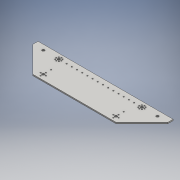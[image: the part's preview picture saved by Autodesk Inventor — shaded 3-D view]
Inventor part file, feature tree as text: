
AUTODESK INVENTOR PART (.ipt)
format: ipt  version: 2016 (Build 200138000, 138)  size: 163,840 bytes
history: native  units: mm
features: reference x46, sketch x2, hole x2, extrude x1
ambient origin geometry x8: Origin, YZ Plane, XZ Plane, XY Plane, X Axis, Y Axis, Z Axis, Center Point
bodies: Body1 (feature_tree)
feature tree (51):
  extrude  "Extrusion2"  Depth=96.0mm
  sketch  "Sketch2"  dims[d0=416.0mm d1=96.0mm]
  sketch  "Sketch3"  dims[d4=4.0mm d5=0.0mm d6=8.0mm d7=6.0mm d8=4.0mm d9=2.0mm d10=90.0deg d11=8.0mm d12=20.594885mm d13=3.7mm d14=6.0mm d15=4.0mm d16=2.0mm d17=90.0deg d18=8.0mm d19=20.594885mm d22=16.0mm d23=80.0mm d24=16.0mm]
  hole  "Hole1"  [1 undecoded]
  hole  "Hole2"  [1 undecoded]
  reference  "Reference1"
  reference  "Reference2"
  reference  "Reference3"
  reference  "Reference4"
  reference  "Reference5"
  reference  "Reference6"
  reference  "Reference7"
  reference  "Reference8"
  reference  "Reference9"
  reference  "Reference10"
  reference  "Reference11"
  reference  "Reference12"
  reference  "Reference13"
  reference  "Reference14"
  reference  "Reference15"
  reference  "Reference16"
  reference  "Reference17"
  reference  "Reference18"
  reference  "Reference19"
  reference  "Reference20"
  reference  "Reference21"
  reference  "Reference22"
  reference  "Reference23"
  reference  "Reference24"
  reference  "Reference25"
  reference  "Reference26"
  reference  "Reference27"
  reference  "Reference28"
  reference  "Reference29"
  reference  "Reference30"
  reference  "Reference31"
  reference  "Reference32"
  reference  "Reference33"
  reference  "Reference34"
  reference  "Reference35"
  reference  "Reference40"
  reference  "Reference41"
  reference  "Reference42"
  reference  "Reference43"
  reference  "Reference44"
  reference  "Reference45"
  reference  "Reference46"
  reference  "Reference47"
  reference  "Reference48"
  reference  "Reference49"
  reference  "Reference50"
note: 2 required parameter values undecoded (feature->parameter linkage not recoverable at this tier; creation-order binding heuristic only, values carry confidence <= 0.55)
